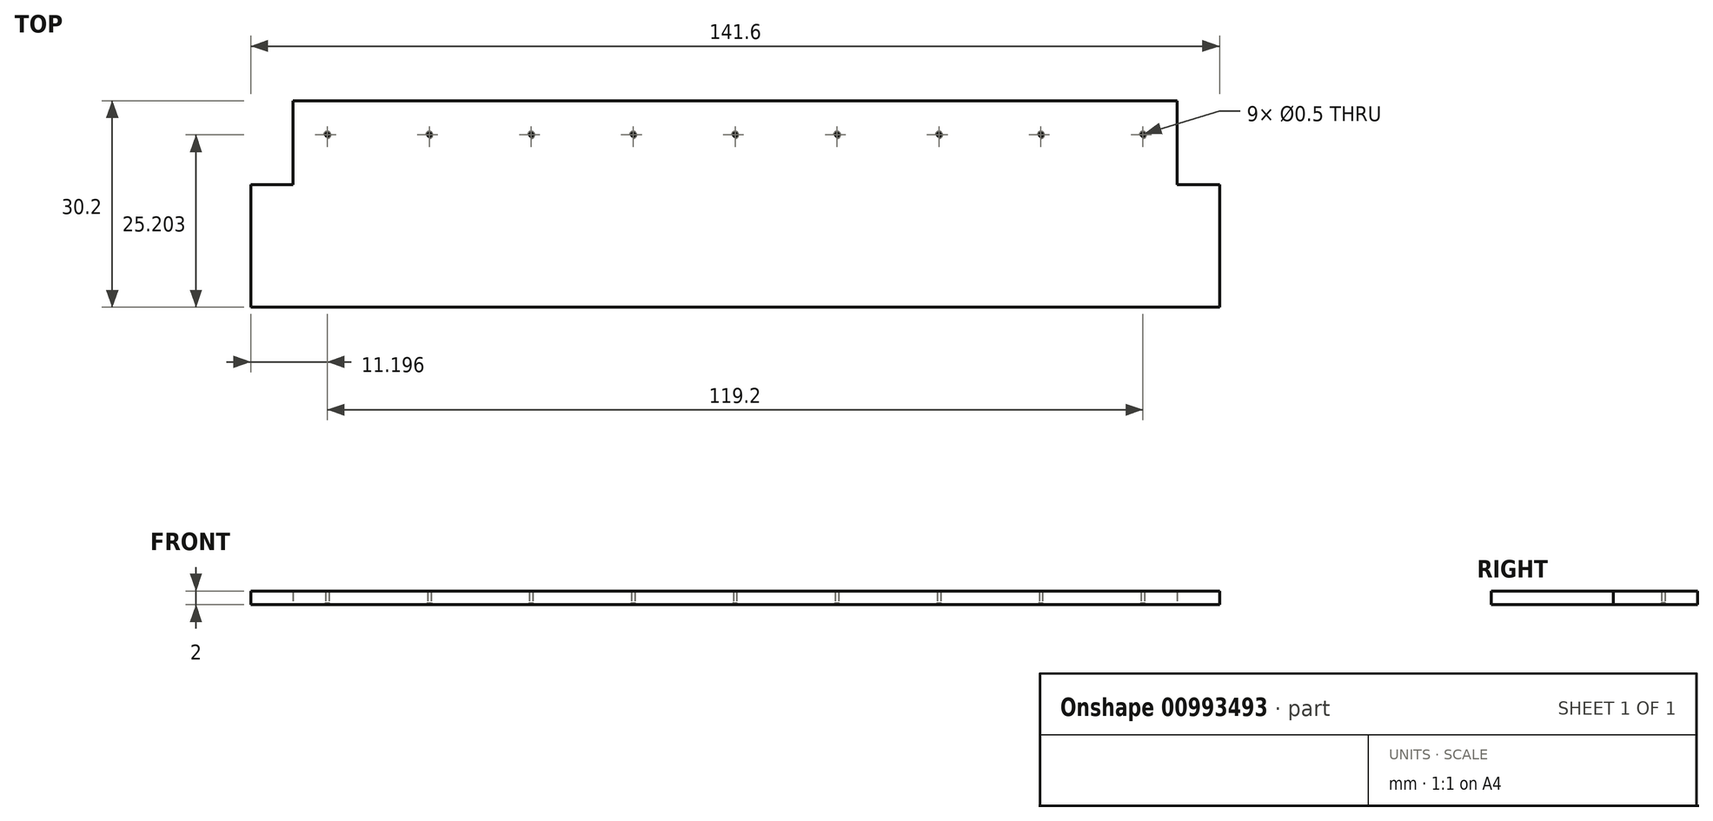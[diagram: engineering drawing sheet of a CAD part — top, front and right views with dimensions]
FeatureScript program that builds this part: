
annotation { "Feature Type Name" : "Feature", "Feature Type Description" : "" }
export const myFeature = defineFeature(function(context is Context, id is Id, definition is map)
    precondition{}
    {
        {
            var Q0;
            Q0=qCreatedBy(makeId("Top.planeOp"),FACE);
            var sketch = newSketch(context, id + "F0", { "sketchPlane" : qUnion([Q0])});
            skLineSegment(sketch, "E0", {"start": v(-37.32, -1.23) * mm, "end": v(-37.32, 16.67) * mm});
            skLineSegment(sketch, "E1", {"start": v(-37.32, 16.67) * mm, "end": v(-31.12, 16.67) * mm});
            skLineSegment(sketch, "E2", {"start": v(-31.12, 16.67) * mm, "end": v(-31.12, 28.97) * mm});
            skLineSegment(sketch, "E3", {"start": v(-31.12, 28.97) * mm, "end": v(98.08, 28.97) * mm});
            skLineSegment(sketch, "E4", {"start": v(98.08, 28.97) * mm, "end": v(98.08, 16.67) * mm});
            skLineSegment(sketch, "E5", {"start": v(98.08, 16.67) * mm, "end": v(104.28, 16.67) * mm});
            skLineSegment(sketch, "E6", {"start": v(104.28, 16.67) * mm, "end": v(104.28, -1.23) * mm});
            skLineSegment(sketch, "E7", {"start": v(104.28, -1.23) * mm, "end": v(-37.32, -1.23) * mm});
            skPoint(sketch, "E8", {"position": v(-11.22, 23.97) * mm});
            skPoint(sketch, "E9", {"position": v(3.68, 23.97) * mm});
            skPoint(sketch, "E10", {"position": v(18.58, 23.97) * mm});
            skPoint(sketch, "E11", {"position": v(-26.12, 23.97) * mm});
            skPoint(sketch, "E12", {"position": v(33.48, 23.97) * mm});
            skPoint(sketch, "E13", {"position": v(48.38, 23.97) * mm});
            skPoint(sketch, "E14", {"position": v(93.08, 23.97) * mm});
            skPoint(sketch, "E15", {"position": v(63.28, 23.97) * mm});
            skPoint(sketch, "E16", {"position": v(78.18, 23.97) * mm});
            skSolve(sketch);
        }
        {
            var Q0;
            Q0=makeQuery(id+"F0.imprint","IMPRINT",FACE,{"disambiguationData":[TD([[makeQuery(id+"F0.imprint","IMPRINT",EDGE,{"derivedFrom":sQuery(id+"F0.wireOp",EDGE,"E0")}),-1.0]])]});
            extrude(context, id + "F1", {"entities" : qUnion([Q0]), "depth" : 2 * mm, "offsetDistance" : 25 * mm});
        }
        {
            var Q0;
            Q0=sQuery(id+"F0.wireOp",VERTEX,"E11");
            var Q1;
            Q1=sQuery(id+"F0.wireOp",VERTEX,"E8");
            var Q2;
            Q2=sQuery(id+"F0.wireOp",VERTEX,"E9");
            var Q3;
            Q3=sQuery(id+"F0.wireOp",VERTEX,"E10");
            var Q4;
            Q4=sQuery(id+"F0.wireOp",VERTEX,"E12");
            var Q5;
            Q5=sQuery(id+"F0.wireOp",VERTEX,"E13");
            var Q6;
            Q6=sQuery(id+"F0.wireOp",VERTEX,"E15");
            var Q7;
            Q7=sQuery(id+"F0.wireOp",VERTEX,"E16");
            var Q8;
            Q8=sQuery(id+"F0.wireOp",VERTEX,"E14");
            var Q9;
            Q9=makeQuery(id+"F1.opExtrude","SWEPT_BODY",BODY,{"disambiguationData":[OSD([sQuery(id+"F0.wireOp",EDGE,"E0"),sQuery(id+"F0.wireOp",EDGE,"E1"),sQuery(id+"F0.wireOp",EDGE,"E2"),sQuery(id+"F0.wireOp",EDGE,"E3"),sQuery(id+"F0.wireOp",EDGE,"E4"),sQuery(id+"F0.wireOp",EDGE,"E5"),sQuery(id+"F0.wireOp",EDGE,"E6"),sQuery(id+"F0.wireOp",EDGE,"E7")])]});
            hole(context, id + "F2", {"style" : HoleStyle.C_SINK, "endStyle" : HoleEndStyle.THROUGH, "oppositeDirection" : true, "holeDiameter" : 0.5 * mm, "cSinkDiameter" : 1 * mm, "cSinkAngle" : 90 * degree, "majorDiameter" : 5 * mm, "isTappedThrough" : true, "tappedDepth" : 12 * mm, "tapClearance" : 3, "locations" : qUnion([Q0, Q1, Q2, Q3, Q4, Q5, Q6, Q7, Q8]), "scope" : qUnion([Q9])});
        }
    });
